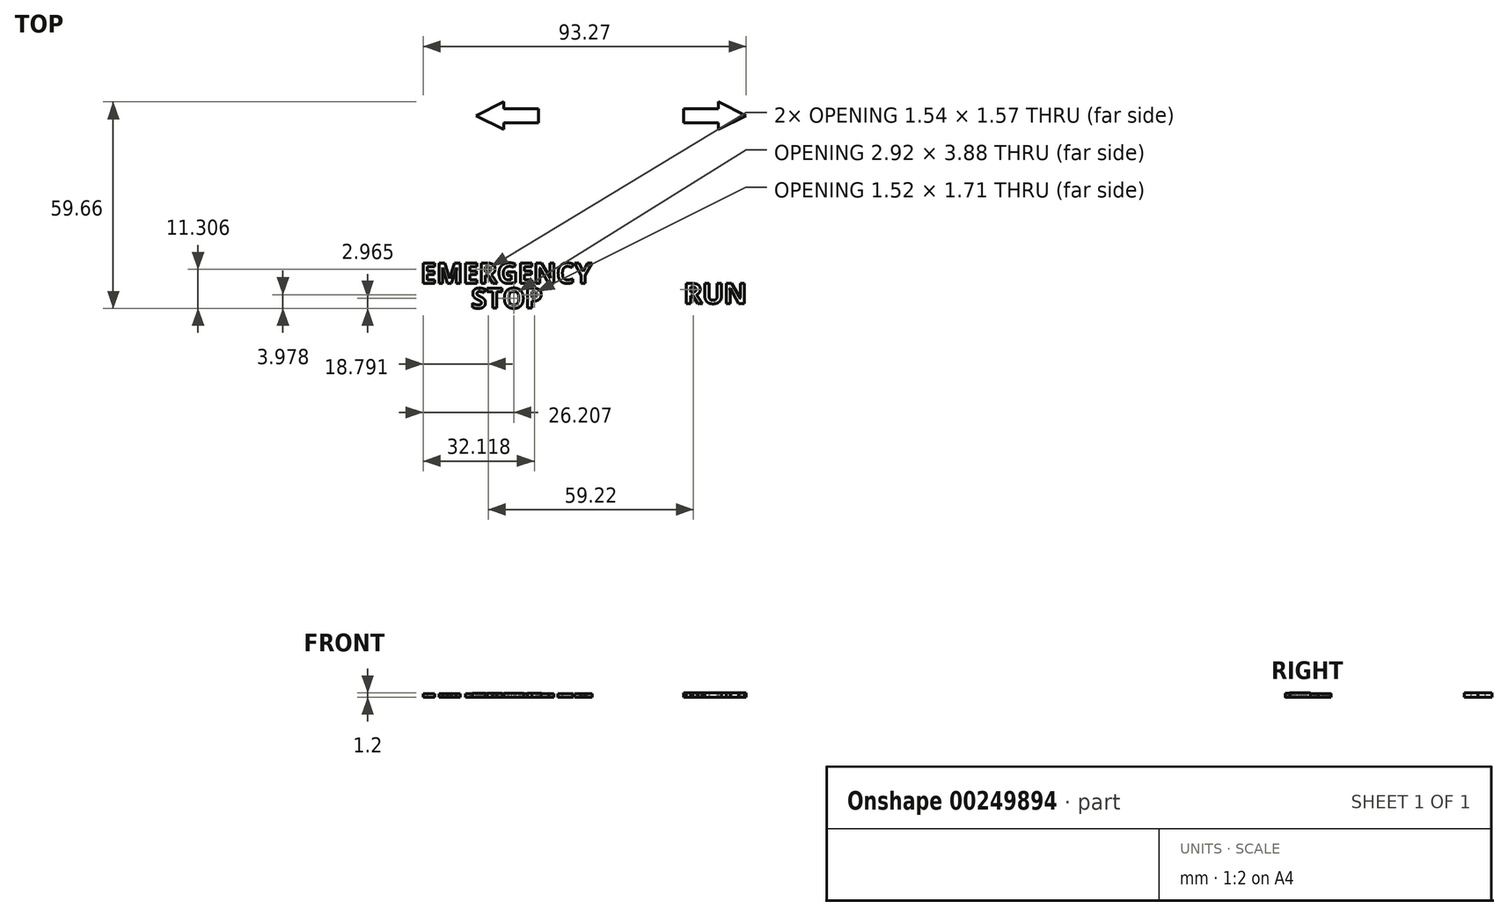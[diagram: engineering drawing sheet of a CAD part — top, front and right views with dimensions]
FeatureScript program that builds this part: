
annotation { "Feature Type Name" : "Feature", "Feature Type Description" : "" }
export const myFeature = defineFeature(function(context is Context, id is Id, definition is map)
    precondition{}
    {
        {
            var Q0;
            Q0=qCreatedBy(makeId("Top.planeOp"),FACE);
            cPlane(context, id + "F0", {"entities" : qUnion([Q0]), "cplaneType" : CPlaneType.OFFSET, "offset" : (4 - 1.2) * mm, "width" : 150 * mm, "height" : 150 * mm});
        }
        {
            var Q0;
            Q0=qCreatedBy(makeId("Top.planeOp"),FACE);
            var sketch = newSketch(context, id + "F1", { "sketchPlane" : qUnion([Q0])});
            skLineSegment(sketch, "E0.bottom", {"start": v(60, -50) * mm, "end": v(-60, -50) * mm});
            skLineSegment(sketch, "E0.top", {"start": v(60, 50) * mm, "end": v(-60, 50) * mm});
            skLineSegment(sketch, "E0.left", {"start": v(60, -50) * mm, "end": v(60, 50) * mm});
            skLineSegment(sketch, "E0.right", {"start": v(-60, -50) * mm, "end": v(-60, 50) * mm});
            skPoint(sketch, "E0.middle", {"position": v(0, 0) * mm});
            skCircle(sketch, "E1", {"center": v(-30, 25) * mm, "radius": 11 * mm});
            skLineSegment(sketch, "E2", {"start": v(0, -50) * mm, "end": v(0, 50) * mm, "construction": true});
            skLineSegment(sketch, "E3", {"start": v(-60, 0) * mm, "end": v(60, 0) * mm, "construction": true});
            skCircle(sketch, "E4.MirrorC", {"center": v(30, 25) * mm, "radius": 11 * mm});
            skCircle(sketch, "E5.MirrorC", {"center": v(30, -25) * mm, "radius": 11 * mm});
            skCircle(sketch, "E6.MirrorC", {"center": v(-30, -25) * mm, "radius": 11 * mm});
            skSolve(sketch);
        }
        {
            var Q0;
            Q0=qCreatedBy(id+"F0.planeOp",FACE);
            var sketch = newSketch(context, id + "F2", { "sketchPlane" : qUnion([Q0])});
            skLineSegment(sketch, "E7", {"start": v(-31, 47) * mm, "end": v(-31, 39) * mm});
            skLineSegment(sketch, "E8", {"start": v(-31, 47) * mm, "end": v(-39, 43) * mm});
            skLineSegment(sketch, "E9", {"start": v(-39, 43) * mm, "end": v(-31, 39) * mm});
            skLineSegment(sketch, "E10.bottom", {"start": v(-31, 45) * mm, "end": v(-21, 45) * mm});
            skLineSegment(sketch, "E10.top", {"start": v(-31, 41) * mm, "end": v(-21, 41) * mm});
            skLineSegment(sketch, "E10.left", {"start": v(-31, 45) * mm, "end": v(-31, 41) * mm});
            skLineSegment(sketch, "E10.right", {"start": v(-21, 45) * mm, "end": v(-21, 41) * mm});
            skLineSegment(sketch, "E11", {"start": v(-21, 43) * mm, "end": v(-39, 43) * mm, "construction": true});
            skLineSegment(sketch, "E12", {"start": v(-30, -4.26) * mm, "end": v(-30, 41) * mm, "construction": true});
            skLineSegment(sketch, "E13.MirrorCS", {"start": v(31, 45) * mm, "end": v(21, 45) * mm});
            skLineSegment(sketch, "E14.MirrorCS", {"start": v(31, 41) * mm, "end": v(21, 41) * mm});
            skLineSegment(sketch, "E15.MirrorCS", {"start": v(21, 45) * mm, "end": v(21, 41) * mm});
            skText(sketch, "E16", { "text": "EMERGENCY", "fontName": "OpenSans-Bold.ttf"});
            skText(sketch, "E17", { "text": "STOP", "fontName": "OpenSans-Bold.ttf"});
            skText(sketch, "E18", { "text": "RUN", "fontName": "OpenSans-Bold.ttf"});
            skLineSegment(sketch, "E19", {"start": v(30, -54.26) * mm, "end": v(30, -2.36) * mm, "construction": true});
            skLineSegment(sketch, "E20", {"start": v(-30, -56.07) * mm, "end": v(-30, -7.74) * mm, "construction": true});
            skLineSegment(sketch, "E21.bottom", {"start": v(60, 50) * mm, "end": v(-60, 50) * mm});
            skLineSegment(sketch, "E21.top", {"start": v(60, -50) * mm, "end": v(-60, -50) * mm});
            skLineSegment(sketch, "E21.left", {"start": v(60, 50) * mm, "end": v(60, -50) * mm});
            skLineSegment(sketch, "E21.right", {"start": v(-60, 50) * mm, "end": v(-60, -50) * mm});
            skPoint(sketch, "E21.middle", {"position": v(0, 0) * mm});
            skLineSegment(sketch, "E22.MirrorCS", {"start": v(31, 47) * mm, "end": v(31, 39) * mm});
            skLineSegment(sketch, "E23.MirrorCS", {"start": v(31, 47) * mm, "end": v(39, 43) * mm});
            skLineSegment(sketch, "E24.MirrorCS", {"start": v(39, 43) * mm, "end": v(31, 39) * mm});
            const initialGuessF2  = {"E16": [-0.055, -0.00537, 1, 0, 0.00586], "E17": [-0.04037, -0.01258, 1, 0, 0.0058], "E18": [0.021, -0.01125, 1, 0, 0.00588]};
            skSetInitialGuess(sketch, initialGuessF2);
            skSolve(sketch);
        }
        {
            var Q0;
            {var subQ1=sQuery(id+"F2.wireOp",EDGE,"E8");Q0=makeQuery(id+"F2.imprint","IMPRINT",FACE,{"disambiguationData":[TD([[makeQuery(id+"F2.imprint","IMPRINT",EDGE,{"derivedFrom":subQ1}),1.0]])]});}
            var Q1;
            Q1=makeQuery(id+"F2.imprint","IMPRINT",FACE,{"disambiguationData":[TD([[makeQuery(id+"F2.imprint","IMPRINT",EDGE,{"derivedFrom":sQuery(id+"F2.wireOp",EDGE,"E10.bottom")}),-1.0]])]});
            var Q2;
            Q2=makeQuery(id+"F2.imprint","IMPRINT",FACE,{"disambiguationData":[TD([[makeQuery(id+"F2.imprint","IMPRINT",EDGE,{"derivedFrom":sQuery(id+"F2.wireOp",EDGE,"E16.sketch_text.stroke-122")}),-1.0]])]});
            var Q3;
            Q3=makeQuery(id+"F2.imprint","IMPRINT",FACE,{"disambiguationData":[TD([[makeQuery(id+"F2.imprint","IMPRINT",EDGE,{"derivedFrom":sQuery(id+"F2.wireOp",EDGE,"E16.sketch_text.stroke-107")}),-1.0]])]});
            var Q4;
            Q4=makeQuery(id+"F2.imprint","IMPRINT",FACE,{"disambiguationData":[TD([[makeQuery(id+"F2.imprint","IMPRINT",EDGE,{"derivedFrom":sQuery(id+"F2.wireOp",EDGE,"E16.sketch_text.stroke-93")}),-1.0]])]});
            var Q5;
            Q5=makeQuery(id+"F2.imprint","IMPRINT",FACE,{"disambiguationData":[TD([[makeQuery(id+"F2.imprint","IMPRINT",EDGE,{"derivedFrom":sQuery(id+"F2.wireOp",EDGE,"E16.sketch_text.stroke-81")}),-1.0]])]});
            var Q6;
            Q6=makeQuery(id+"F2.imprint","IMPRINT",FACE,{"disambiguationData":[TD([[makeQuery(id+"F2.imprint","IMPRINT",EDGE,{"derivedFrom":sQuery(id+"F2.wireOp",EDGE,"E16.sketch_text.stroke-62")}),-1.0]])]});
            var Q7;
            Q7=makeQuery(id+"F2.imprint","IMPRINT",FACE,{"disambiguationData":[TD([[makeQuery(id+"F2.imprint","IMPRINT",EDGE,{"derivedFrom":sQuery(id+"F2.wireOp",EDGE,"E16.sketch_text.stroke-43")}),-1.0]])]});
            var Q8;
            Q8=makeQuery(id+"F2.imprint","IMPRINT",FACE,{"disambiguationData":[TD([[makeQuery(id+"F2.imprint","IMPRINT",EDGE,{"derivedFrom":sQuery(id+"F2.wireOp",EDGE,"E16.sketch_text.stroke-31")}),-1.0]])]});
            var Q9;
            Q9=makeQuery(id+"F2.imprint","IMPRINT",FACE,{"disambiguationData":[TD([[makeQuery(id+"F2.imprint","IMPRINT",EDGE,{"derivedFrom":sQuery(id+"F2.wireOp",EDGE,"E16.sketch_text.stroke-12")}),-1.0]])]});
            var Q10;
            Q10=makeQuery(id+"F2.imprint","IMPRINT",FACE,{"disambiguationData":[TD([[makeQuery(id+"F2.imprint","IMPRINT",EDGE,{"derivedFrom":sQuery(id+"F2.wireOp",EDGE,"E16.sketch_text.stroke-0")}),-1.0]])]});
            extrude(context, id + "F3", {"entities" : qUnion([Q0, Q1, Q2, Q3, Q4, Q5, Q6, Q7, Q8, Q9, Q10]), "depth" : 1 * mm});
        }
        {
            var Q0;
            Q0=makeQuery(id+"F2.imprint","IMPRINT",FACE,{"disambiguationData":[TD([[makeQuery(id+"F2.imprint","IMPRINT",EDGE,{"derivedFrom":sQuery(id+"F2.wireOp",EDGE,"E17.sketch_text.stroke-0")}),-1.0]])]});
            var Q1;
            Q1=makeQuery(id+"F2.imprint","IMPRINT",FACE,{"disambiguationData":[TD([[makeQuery(id+"F2.imprint","IMPRINT",EDGE,{"derivedFrom":sQuery(id+"F2.wireOp",EDGE,"E17.sketch_text.stroke-28")}),-1.0]])]});
            var Q2;
            Q2=makeQuery(id+"F2.imprint","IMPRINT",FACE,{"disambiguationData":[TD([[makeQuery(id+"F2.imprint","IMPRINT",EDGE,{"derivedFrom":sQuery(id+"F2.wireOp",EDGE,"E17.sketch_text.stroke-36")}),-1.0]])]});
            var Q3;
            Q3=makeQuery(id+"F2.imprint","IMPRINT",FACE,{"disambiguationData":[TD([[makeQuery(id+"F2.imprint","IMPRINT",EDGE,{"derivedFrom":sQuery(id+"F2.wireOp",EDGE,"E17.sketch_text.stroke-50")}),-1.0]])]});
            extrude(context, id + "F4", {"entities" : qUnion([Q0, Q1, Q2, Q3]), "depth" : 1.1 * mm});
        }
        {
            var Q0;
            Q0=makeQuery(id+"F2.imprint","IMPRINT",FACE,{"disambiguationData":[TD([[makeQuery(id+"F2.imprint","IMPRINT",EDGE,{"derivedFrom":sQuery(id+"F2.wireOp",EDGE,"E18.sketch_text.stroke-34")}),-1.0]])]});
            var Q1;
            Q1=makeQuery(id+"F2.imprint","IMPRINT",FACE,{"disambiguationData":[TD([[makeQuery(id+"F2.imprint","IMPRINT",EDGE,{"derivedFrom":sQuery(id+"F2.wireOp",EDGE,"E18.sketch_text.stroke-19")}),-1.0]])]});
            var Q2;
            Q2=makeQuery(id+"F2.imprint","IMPRINT",FACE,{"disambiguationData":[TD([[makeQuery(id+"F2.imprint","IMPRINT",EDGE,{"derivedFrom":sQuery(id+"F2.wireOp",EDGE,"E18.sketch_text.stroke-0")}),-1.0]])]});
            var Q3;
            {var subQ0=sQuery(id+"F2.wireOp",EDGE,"E23.MirrorCS");Q3=makeQuery(id+"F2.imprint","IMPRINT",FACE,{"disambiguationData":[TD([[makeQuery(id+"F2.imprint","IMPRINT",EDGE,{"derivedFrom":subQ0}),-1.0]])]});}
            var Q4;
            {var subQ0=sQuery(id+"F2.wireOp",EDGE,"E13.MirrorCS");Q4=makeQuery(id+"F2.imprint","IMPRINT",FACE,{"disambiguationData":[TD([[makeQuery(id+"F2.imprint","IMPRINT",EDGE,{"derivedFrom":subQ0}),1.0]])]});}
            extrude(context, id + "F5", {"entities" : qUnion([Q0, Q1, Q2, Q3, Q4]), "depth" : 1.2 * mm});
        }
    });
